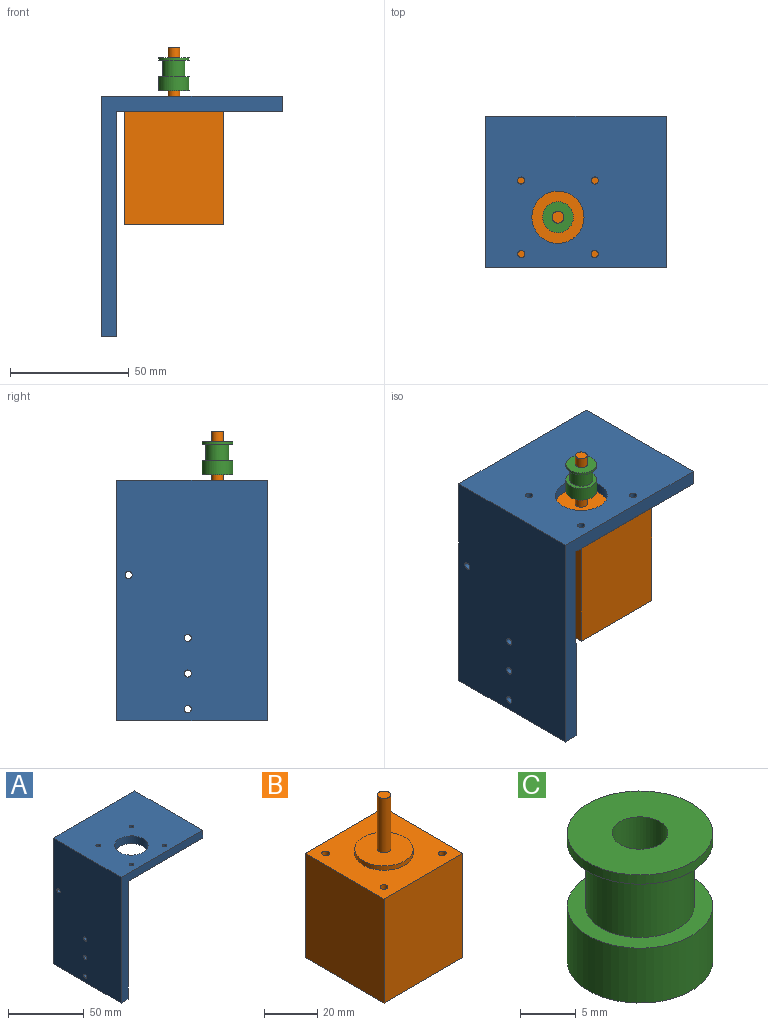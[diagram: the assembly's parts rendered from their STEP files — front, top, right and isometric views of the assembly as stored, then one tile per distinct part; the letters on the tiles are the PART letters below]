
ASSEMBLY  parts=3 mates=4
PART A: 17 faces, bbox 76.2x63.5x101.6 mm
  f0: cylinder r=1.5mm len=6.35mm, axis (1,0,0), area 59.8mm2, adj f2,f4
  f1: cylinder r=1.5mm len=6.35mm, axis (1,0,0), area 59.8mm2, adj f2,f4
  f2: plane 101.6x63.5mm, normal (-1,0,0), area 6423.3mm2, adj f0,f1,f3,f7,f8,f9,f15,f16
  f3: plane 63.5x6.35mm, normal (0,0,-1), area 403.2mm2, adj f2,f4,f8,f9
  f4: plane 95.25x63.5mm, normal (1,0,0), area 6020.1mm2, adj f0,f1,f3,f5,f8,f9,f15,f16
  f5: plane 69.85x63.5mm, normal (0,0,-1), area 4027.1mm2, adj f4,f6,f8,f9,f10,f11,f12,f13
  f6: plane 63.5x6.35mm, normal (1,0,0), area 403.2mm2, adj f5,f7,f8,f9
  f7: plane 76.2x63.5mm, normal (0,0,1), area 4430.3mm2, adj f2,f6,f8,f9,f10,f11,f12,f13
  f8: plane 101.6x76.2mm, normal (0,-1,0), area 1088.7mm2, adj f2,f3,f4,f5,f6,f7
  f9: plane 101.6x76.2mm, normal (0,1,0), area 1088.7mm2, adj f2,f3,f4,f5,f6,f7
  f10: cylinder r=11mm len=22mm, axis (0,0,1), area 438.9mm2, adj f5,f7
  f11: cylinder r=1.5mm len=6.35mm, axis (0,0,1), area 59.8mm2, adj f5,f7
  f12: cylinder r=1.5mm len=6.35mm, axis (0,0,1), area 59.8mm2, adj f5,f7
  f13: cylinder r=1.5mm len=6.35mm, axis (0,0,1), area 59.8mm2, adj f5,f7
  f14: cylinder r=1.5mm len=6.35mm, axis (0,0,1), area 59.8mm2, adj f5,f7
  f15: cylinder r=1.5mm len=6.35mm, axis (1,0,0), area 59.8mm2, adj f2,f4
  f16: cylinder r=1.5mm len=6.35mm, axis (1,0,0), area 59.8mm2, adj f2,f4
PART B: 18 faces, bbox 42x42x75 mm
  f0: plane 48x42mm, normal (1,0,0), area 2016mm2, adj f1,f3,f4,f5
  f1: plane 48x42mm, normal (0,1,0), area 2016mm2, adj f0,f2,f4,f5
  f2: plane 48x42mm, normal (-1,0,0), area 2016mm2, adj f1,f3,f4,f5
  f3: plane 48x42mm, normal (0,-1,0), area 2016mm2, adj f0,f2,f4,f5
  f4: plane 42x42mm, normal (0,0,1), area 1355.6mm2, adj f0,f1,f2,f3,f6,f10,f12,f14
  f5: plane 42x42mm, normal (0,0,-1), area 1764mm2, adj f0,f1,f2,f3
  f6: cylinder r=11mm len=22mm, axis (0,0,-1), area 138.2mm2, adj f4,f7
  f7: plane 22x22mm, normal (0,0,1), area 360.5mm2, adj f6,f8
  f8: cylinder r=2.5mm len=25mm, axis (0,0,-1), area 392.7mm2, adj f7,f9
  f9: plane 5x5mm, normal (0,0,1), area 19.6mm2, adj f8
  f10: cylinder r=1.5mm len=10mm, axis (0,0,1), area 94.2mm2, adj f4,f11
  f11: plane 3x3mm, normal (0,0,1), area 7.1mm2, adj f10
  f12: cylinder r=1.5mm len=10mm, axis (0,0,1), area 94.2mm2, adj f4,f13
  f13: plane 3x3mm, normal (0,0,1), area 7.1mm2, adj f12
  f14: cylinder r=1.5mm len=10mm, axis (0,0,1), area 94.2mm2, adj f4,f15
  f15: plane 3x3mm, normal (0,0,1), area 7.1mm2, adj f14
  f16: cylinder r=1.5mm len=10mm, axis (0,0,1), area 94.2mm2, adj f4,f17
  f17: plane 3x3mm, normal (0,0,1), area 7.1mm2, adj f16
PART C: 8 faces, bbox 13x13x14 mm
  f0: plane 13x13mm, normal (0,0,-1), area 113.1mm2, adj f1,f7
  f1: cylinder r=2.5mm len=14mm, axis (0,0,-1), area 219.9mm2, adj f0,f2
  f2: plane 13x13mm, normal (0,0,1), area 113.1mm2, adj f1,f3
  f3: cylinder r=6.5mm len=13mm, axis (0,0,-1), area 40.8mm2, adj f2,f4
  f4: plane 13x13mm, normal (0,0,-1), area 58.8mm2, adj f3,f5
  f5: cylinder r=4.85mm len=9.7mm, axis (0,0,-1), area 213.3mm2, adj f4,f6
  f6: plane 13x13mm, normal (0,0,1), area 58.8mm2, adj f5,f7
  f7: cylinder r=6.5mm len=13mm, axis (0,0,-1), area 245mm2, adj f0,f6
PLACE A t=(-80.8,-5.51,-31.56)mm
PLACE B t=(-50.3,-48.01,15.69)mm
PLACE C t=(-50.3,-48.01,72.19)mm
MATE cylindrical B.f14 <-> A.f13  axis (0,0,1) through (-65.8,-63.51,63.69)mm
MATE cylindrical C.f1 <-> B.f8  axis (0,0,1) through (-50.3,-48.01,78.19)mm
MATE cylindrical B.f8 <-> A.f10  axis (0,0,-1) through (-50.3,-48.01,65.69)mm
MATE planar B.f6 <-> A.f5  axis (0,0,1) through (-50.3,-48.01,63.69)mm
